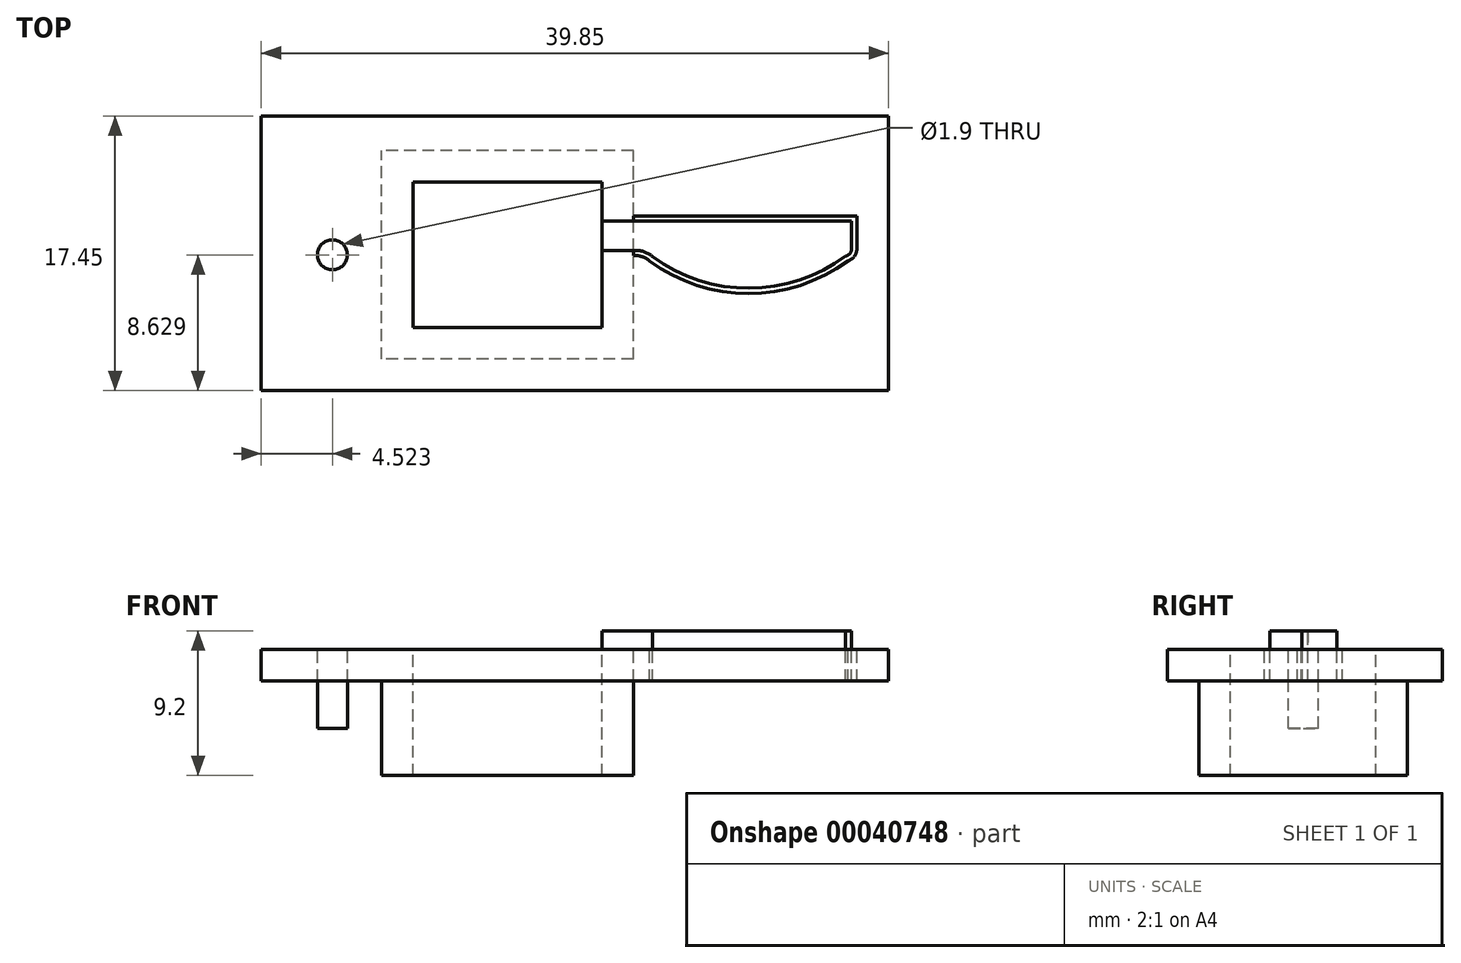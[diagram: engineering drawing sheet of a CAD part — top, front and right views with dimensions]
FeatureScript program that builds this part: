
annotation { "Feature Type Name" : "Feature", "Feature Type Description" : "" }
export const myFeature = defineFeature(function(context is Context, id is Id, definition is map)
    precondition{}
    {
        {
            var Q0;
            Q0=qCreatedBy(makeId("Top.planeOp"),FACE);
            var sketch = newSketch(context, id + "F0", { "sketchPlane" : qUnion([Q0])});
            skLineSegment(sketch, "E0", {"start": v(-14.38, 0) * mm, "end": v(14.38, 0) * mm});
            skLineSegment(sketch, "E1", {"start": v(14.38, 0) * mm, "end": v(14.38, -2.1) * mm});
            skLineSegment(sketch, "E2", {"start": v(-14.38, 0) * mm, "end": v(-14.38, -4.57) * mm});
            skLineSegment(sketch, "E3", {"start": v(-14.38, -4.57) * mm, "end": v(-4.8, -4.57) * mm});
            skLineSegment(sketch, "E4", {"start": v(-1.54, -2.52) * mm, "end": v(0.32, -2.52) * mm});
            skPoint(sketch, "E5", {"position": v(0, 0) * mm});
            skArc(sketch, "E6", {"start": v(-4.8, -4.57) * mm, "mid": v(-4.48, -4.53) * mm, "end": v(-4.18, -4.4) * mm});
            skArc(sketch, "E7", {"start": v(-1.54, -2.52) * mm, "mid": v(-2.14, -2.6) * mm, "end": v(-2.69, -2.86) * mm});
            skLineSegment(sketch, "E8", {"start": v(-4.18, -4.4) * mm, "end": v(-2.69, -2.86) * mm});
            skArc(sketch, "E9", {"start": v(0.32, -2.52) * mm, "mid": v(0.8, -2.6) * mm, "end": v(1.2, -2.85) * mm});
            skArc(sketch, "E10", {"start": v(1.2, -2.85) * mm, "mid": v(7.5, -4.93) * mm, "end": v(13.81, -2.85) * mm});
            skArc(sketch, "E11", {"start": v(14.38, -2.1) * mm, "mid": v(14.22, -2.57) * mm, "end": v(13.81, -2.85) * mm});
            skSolve(sketch);
        }
        {
            var Q0;
            Q0=qCreatedBy(makeId("Top.planeOp"),FACE);
            var sketch = newSketch(context, id + "F1", { "sketchPlane" : qUnion([Q0])});
            skLineSegment(sketch, "E12.rect.bottom", {"start": v(-1.81, -7.1) * mm, "end": v(-13.81, -7.1) * mm});
            skLineSegment(sketch, "E12.rect.top", {"start": v(-1.81, 2.15) * mm, "end": v(-13.81, 2.15) * mm});
            skLineSegment(sketch, "E12.rect.left", {"start": v(-1.81, -7.1) * mm, "end": v(-1.81, 2.15) * mm});
            skLineSegment(sketch, "E12.rect.right", {"start": v(-13.81, -7.1) * mm, "end": v(-13.81, 2.15) * mm});
            skPoint(sketch, "E12.rect.middle", {"position": v(-7.81, -2.47) * mm});
            skLineSegment(sketch, "E13.bottom", {"start": v(16.4, 6.35) * mm, "end": v(-23.45, 6.35) * mm});
            skLineSegment(sketch, "E13.top", {"start": v(16.4, -11.1) * mm, "end": v(-23.45, -11.1) * mm});
            skLineSegment(sketch, "E13.left", {"start": v(16.4, 6.35) * mm, "end": v(16.4, -11.1) * mm});
            skLineSegment(sketch, "E13.right", {"start": v(-23.45, 6.35) * mm, "end": v(-23.45, -11.1) * mm});
            skLineSegment(sketch, "E14.0.0", {"start": v(14.38, 0) * mm, "end": v(-14.38, 0) * mm});
            skLineSegment(sketch, "E14.0.1", {"start": v(-14.38, 0) * mm, "end": v(-14.38, -4.57) * mm});
            skLineSegment(sketch, "E14.0.2", {"start": v(-14.38, -4.57) * mm, "end": v(-4.8, -4.57) * mm});
            skArc(sketch, "E14.0.3", {"start": v(-4.8, -4.57) * mm, "mid": v(-4.48, -4.53) * mm, "end": v(-4.18, -4.4) * mm});
            skLineSegment(sketch, "E14.0.4", {"start": v(-4.18, -4.4) * mm, "end": v(-2.69, -2.86) * mm});
            skArc(sketch, "E14.0.5", {"start": v(-2.69, -2.86) * mm, "mid": v(-2.14, -2.6) * mm, "end": v(-1.54, -2.52) * mm});
            skLineSegment(sketch, "E14.0.6", {"start": v(-1.54, -2.52) * mm, "end": v(0.32, -2.52) * mm});
            skArc(sketch, "E14.0.7", {"start": v(0.32, -2.52) * mm, "mid": v(0.8, -2.6) * mm, "end": v(1.2, -2.85) * mm});
            skArc(sketch, "E14.0.8", {"start": v(1.2, -2.85) * mm, "mid": v(7.5, -4.93) * mm, "end": v(13.81, -2.85) * mm});
            skArc(sketch, "E14.0.9", {"start": v(13.81, -2.85) * mm, "mid": v(14.22, -2.57) * mm, "end": v(14.38, -2.1) * mm});
            skLineSegment(sketch, "E14.0.10", {"start": v(14.38, -2.1) * mm, "end": v(14.38, 0) * mm});
            skLineSegment(sketch, "E15.0", {"start": v(-14.05, -0.33) * mm, "end": v(-14.05, -4.24) * mm});
            skLineSegment(sketch, "E15.1", {"start": v(14.05, -0.33) * mm, "end": v(-14.05, -0.33) * mm});
            skLineSegment(sketch, "E15.2", {"start": v(14.05, -2.1) * mm, "end": v(14.05, -0.33) * mm});
            skArc(sketch, "E15.3", {"start": v(13.67, -2.55) * mm, "mid": v(13.94, -2.39) * mm, "end": v(14.05, -2.1) * mm});
            skArc(sketch, "E15.4", {"start": v(1.41, -2.6) * mm, "mid": v(7.55, -4.6) * mm, "end": v(13.67, -2.55) * mm});
            skLineSegment(sketch, "E15.5", {"start": v(-14.05, -4.24) * mm, "end": v(-4.8, -4.24) * mm});
            skArc(sketch, "E15.6", {"start": v(-4.8, -4.24) * mm, "mid": v(-4.37, -4.12) * mm, "end": v(-4.07, -3.8) * mm});
            skLineSegment(sketch, "E15.7", {"start": v(-4.07, -3.8) * mm, "end": v(-2.9, -2.6) * mm});
            skArc(sketch, "E15.8", {"start": v(-2.9, -2.6) * mm, "mid": v(-2.25, -2.3) * mm, "end": v(-1.54, -2.19) * mm});
            skLineSegment(sketch, "E15.9", {"start": v(-1.54, -2.19) * mm, "end": v(0.32, -2.19) * mm});
            skArc(sketch, "E15.10", {"start": v(0.32, -2.19) * mm, "mid": v(0.9, -2.3) * mm, "end": v(1.41, -2.6) * mm});
            skLineSegment(sketch, "E16.0", {"start": v(0.19, 4.15) * mm, "end": v(-15.81, 4.15) * mm});
            skLineSegment(sketch, "E16.1", {"start": v(0.19, -9.1) * mm, "end": v(0.19, 4.15) * mm});
            skLineSegment(sketch, "E16.2", {"start": v(0.19, -9.1) * mm, "end": v(-15.81, -9.1) * mm});
            skLineSegment(sketch, "E16.3", {"start": v(-15.81, -9.1) * mm, "end": v(-15.81, 4.15) * mm});
            skSolve(sketch);
        }
        {
            var Q0;
            {var subQ6=sQuery(id+"F1.wireOp",EDGE,"E15.2");Q0=makeQuery(id+"F1.imprint","IMPRINT",FACE,{"disambiguationData":[TD([[makeQuery(id+"F1.imprint","IMPRINT",EDGE,{"derivedFrom":subQ6}),1.0]])]});}
            var Q1;
            Q1=makeQuery(id+"F1.imprint","IMPRINT",FACE,{"disambiguationData":[TD([[makeQuery(id+"F1.imprint","IMPRINT",EDGE,{"derivedFrom":sQuery(id+"F1.wireOp",EDGE,"E13.bottom")}),1.0]])]});
            var Q2;
            {var subQ17=sQuery(id+"F1.wireOp",EDGE,"E12.rect.bottom");Q2=makeQuery(id+"F1.imprint","IMPRINT",FACE,{"disambiguationData":[TD([[makeQuery(id+"F1.imprint","IMPRINT",EDGE,{"derivedFrom":subQ17}),1.0]])]});}
            var Q3;
            {var subQ2=sQuery(id+"F1.wireOp",EDGE,"E12.rect.bottom");Q3=makeQuery(id+"F1.imprint","IMPRINT",FACE,{"disambiguationData":[TD([[makeQuery(id+"F1.imprint","IMPRINT",EDGE,{"derivedFrom":subQ2}),-1.0]])]});}
            var Q4;
            {var subQ5=sQuery(id+"F1.wireOp",EDGE,"E12.rect.top");Q4=makeQuery(id+"F1.imprint","IMPRINT",FACE,{"disambiguationData":[TD([[makeQuery(id+"F1.imprint","IMPRINT",EDGE,{"derivedFrom":subQ5}),1.0]])]});}
            var Q5;
            {var subQ1=sQuery(id+"F1.wireOp",EDGE,"E15.6");Q5=makeQuery(id+"F1.imprint","IMPRINT",FACE,{"disambiguationData":[TD([[makeQuery(id+"F1.imprint","IMPRINT",EDGE,{"derivedFrom":subQ1}),1.0]])]});}
            var Q6;
            {var subQ5=sQuery(id+"F1.wireOp",EDGE,"E15.8");var subQ7=sQuery(id+"F1.wireOp",EDGE,"E12.rect.left");var subQ9=makeQuery(id+"F1.imprint","INTERSECT",VERTEX,{"derivedFrom":[subQ7,subQ5]});Q6=makeQuery(id+"F1.imprint","IMPRINT",FACE,{"disambiguationData":[TD([[makeQuery(id+"F1.imprint","IMPRINT",EDGE,{"disambiguationData":[TD([[subQ9,-1.0]])],"derivedFrom":subQ7}),-1.0]])]});}
            var Q7;
            {var subQ0=sQuery(id+"F1.wireOp",EDGE,"E15.1");var subQ3=sQuery(id+"F1.wireOp",EDGE,"E12.rect.left");var subQ4=makeQuery(id+"F1.imprint","INTERSECT",VERTEX,{"derivedFrom":[subQ3,subQ0]});Q7=makeQuery(id+"F1.imprint","IMPRINT",FACE,{"disambiguationData":[TD([[makeQuery(id+"F1.imprint","IMPRINT",EDGE,{"disambiguationData":[TD([[subQ4,-1.0]])],"derivedFrom":subQ3}),-1.0]])]});}
            var Q8;
            {var subQ0=sQuery(id+"F1.wireOp",EDGE,"E15.1");var subQ3=sQuery(id+"F1.wireOp",EDGE,"E12.rect.left");var subQ4=makeQuery(id+"F1.imprint","INTERSECT",VERTEX,{"derivedFrom":[subQ3,subQ0]});Q8=makeQuery(id+"F1.imprint","IMPRINT",FACE,{"disambiguationData":[TD([[makeQuery(id+"F1.imprint","IMPRINT",EDGE,{"disambiguationData":[TD([[subQ4,-1.0]])],"derivedFrom":subQ3}),1.0]])]});}
            var Q9;
            {var subQ3=sQuery(id+"F1.wireOp",EDGE,"E15.0");Q9=makeQuery(id+"F1.imprint","IMPRINT",FACE,{"disambiguationData":[TD([[makeQuery(id+"F1.imprint","IMPRINT",EDGE,{"derivedFrom":subQ3}),1.0]])]});}
            var Q10;
            {var subQ10=sQuery(id+"F1.wireOp",EDGE,"E14.0.7");Q10=makeQuery(id+"F1.imprint","IMPRINT",FACE,{"disambiguationData":[TD([[makeQuery(id+"F1.imprint","IMPRINT",EDGE,{"derivedFrom":subQ10}),1.0]])]});}
            var Q11;
            {var subQ13=sQuery(id+"F1.wireOp",EDGE,"E14.0.3");Q11=makeQuery(id+"F1.imprint","IMPRINT",FACE,{"disambiguationData":[TD([[makeQuery(id+"F1.imprint","IMPRINT",EDGE,{"derivedFrom":subQ13}),1.0]])]});}
            var Q12;
            {var subQ6=sQuery(id+"F1.wireOp",EDGE,"E14.0.1");Q12=makeQuery(id+"F1.imprint","IMPRINT",FACE,{"disambiguationData":[TD([[makeQuery(id+"F1.imprint","IMPRINT",EDGE,{"derivedFrom":subQ6}),1.0]])]});}
            var Q13;
            {var subQ5=sQuery(id+"F1.wireOp",EDGE,"E12.rect.left");var subQ7=sQuery(id+"F1.wireOp",EDGE,"E14.0.5");var subQ8=makeQuery(id+"F1.imprint","INTERSECT",VERTEX,{"derivedFrom":[subQ5,subQ7]});Q13=makeQuery(id+"F1.imprint","IMPRINT",FACE,{"disambiguationData":[TD([[makeQuery(id+"F1.imprint","IMPRINT",EDGE,{"disambiguationData":[TD([[subQ8,-1.0]])],"derivedFrom":subQ5}),-1.0]])]});}
            extrude(context, id + "F2", {"entities" : qUnion([Q0, Q1, Q2, Q3, Q4, Q5, Q6, Q7, Q8, Q9, Q10, Q11, Q12, Q13]), "oppositeDirection" : true, "depth" : 2 * mm});
        }
        {
            var Q0;
            {var subQ17=sQuery(id+"F1.wireOp",EDGE,"E12.rect.bottom");Q0=makeQuery(id+"F1.imprint","IMPRINT",FACE,{"disambiguationData":[TD([[makeQuery(id+"F1.imprint","IMPRINT",EDGE,{"derivedFrom":subQ17}),1.0]])]});}
            var Q1;
            {var subQ1=sQuery(id+"F1.wireOp",EDGE,"E15.6");Q1=makeQuery(id+"F1.imprint","IMPRINT",FACE,{"disambiguationData":[TD([[makeQuery(id+"F1.imprint","IMPRINT",EDGE,{"derivedFrom":subQ1}),1.0]])]});}
            var Q2;
            {var subQ5=sQuery(id+"F1.wireOp",EDGE,"E15.8");var subQ7=sQuery(id+"F1.wireOp",EDGE,"E12.rect.left");var subQ9=makeQuery(id+"F1.imprint","INTERSECT",VERTEX,{"derivedFrom":[subQ7,subQ5]});Q2=makeQuery(id+"F1.imprint","IMPRINT",FACE,{"disambiguationData":[TD([[makeQuery(id+"F1.imprint","IMPRINT",EDGE,{"disambiguationData":[TD([[subQ9,-1.0]])],"derivedFrom":subQ7}),-1.0]])]});}
            var Q3;
            {var subQ0=sQuery(id+"F1.wireOp",EDGE,"E15.1");var subQ3=sQuery(id+"F1.wireOp",EDGE,"E12.rect.left");var subQ4=makeQuery(id+"F1.imprint","INTERSECT",VERTEX,{"derivedFrom":[subQ3,subQ0]});Q3=makeQuery(id+"F1.imprint","IMPRINT",FACE,{"disambiguationData":[TD([[makeQuery(id+"F1.imprint","IMPRINT",EDGE,{"disambiguationData":[TD([[subQ4,-1.0]])],"derivedFrom":subQ3}),-1.0]])]});}
            var Q4;
            {var subQ0=sQuery(id+"F1.wireOp",EDGE,"E15.1");var subQ3=sQuery(id+"F1.wireOp",EDGE,"E12.rect.left");var subQ4=makeQuery(id+"F1.imprint","INTERSECT",VERTEX,{"derivedFrom":[subQ3,subQ0]});Q4=makeQuery(id+"F1.imprint","IMPRINT",FACE,{"disambiguationData":[TD([[makeQuery(id+"F1.imprint","IMPRINT",EDGE,{"disambiguationData":[TD([[subQ4,-1.0]])],"derivedFrom":subQ3}),1.0]])]});}
            var Q5;
            {var subQ5=sQuery(id+"F1.wireOp",EDGE,"E12.rect.top");Q5=makeQuery(id+"F1.imprint","IMPRINT",FACE,{"disambiguationData":[TD([[makeQuery(id+"F1.imprint","IMPRINT",EDGE,{"derivedFrom":subQ5}),1.0]])]});}
            var Q6;
            {var subQ13=sQuery(id+"F1.wireOp",EDGE,"E14.0.3");Q6=makeQuery(id+"F1.imprint","IMPRINT",FACE,{"disambiguationData":[TD([[makeQuery(id+"F1.imprint","IMPRINT",EDGE,{"derivedFrom":subQ13}),1.0]])]});}
            var Q7;
            {var subQ2=sQuery(id+"F1.wireOp",EDGE,"E12.rect.bottom");Q7=makeQuery(id+"F1.imprint","IMPRINT",FACE,{"disambiguationData":[TD([[makeQuery(id+"F1.imprint","IMPRINT",EDGE,{"derivedFrom":subQ2}),-1.0]])]});}
            var Q8;
            {var subQ5=sQuery(id+"F1.wireOp",EDGE,"E12.rect.left");var subQ7=sQuery(id+"F1.wireOp",EDGE,"E14.0.5");var subQ8=makeQuery(id+"F1.imprint","INTERSECT",VERTEX,{"derivedFrom":[subQ5,subQ7]});Q8=makeQuery(id+"F1.imprint","IMPRINT",FACE,{"disambiguationData":[TD([[makeQuery(id+"F1.imprint","IMPRINT",EDGE,{"disambiguationData":[TD([[subQ8,-1.0]])],"derivedFrom":subQ5}),-1.0]])]});}
            var Q9;
            {var subQ6=sQuery(id+"F1.wireOp",EDGE,"E14.0.1");Q9=makeQuery(id+"F1.imprint","IMPRINT",FACE,{"disambiguationData":[TD([[makeQuery(id+"F1.imprint","IMPRINT",EDGE,{"derivedFrom":subQ6}),1.0]])]});}
            var Q10;
            {var subQ3=sQuery(id+"F1.wireOp",EDGE,"E15.0");Q10=makeQuery(id+"F1.imprint","IMPRINT",FACE,{"disambiguationData":[TD([[makeQuery(id+"F1.imprint","IMPRINT",EDGE,{"derivedFrom":subQ3}),1.0]])]});}
            extrude(context, id + "F3", {"entities" : qUnion([Q0, Q1, Q2, Q3, Q4, Q5, Q6, Q7, Q8, Q9, Q10]), "operationType" : NewBodyOperationType.ADD, "oppositeDirection" : true, "depth" : 8 * mm});
        }
        {
            var Q0;
            {var subQ1=sQuery(id+"F1.wireOp",EDGE,"E15.6");Q0=makeQuery(id+"F1.imprint","IMPRINT",FACE,{"disambiguationData":[TD([[makeQuery(id+"F1.imprint","IMPRINT",EDGE,{"derivedFrom":subQ1}),1.0]])]});}
            var Q1;
            {var subQ5=sQuery(id+"F1.wireOp",EDGE,"E15.8");var subQ7=sQuery(id+"F1.wireOp",EDGE,"E12.rect.left");var subQ9=makeQuery(id+"F1.imprint","INTERSECT",VERTEX,{"derivedFrom":[subQ7,subQ5]});Q1=makeQuery(id+"F1.imprint","IMPRINT",FACE,{"disambiguationData":[TD([[makeQuery(id+"F1.imprint","IMPRINT",EDGE,{"disambiguationData":[TD([[subQ9,-1.0]])],"derivedFrom":subQ7}),-1.0]])]});}
            var Q2;
            {var subQ6=sQuery(id+"F1.wireOp",EDGE,"E15.2");Q2=makeQuery(id+"F1.imprint","IMPRINT",FACE,{"disambiguationData":[TD([[makeQuery(id+"F1.imprint","IMPRINT",EDGE,{"derivedFrom":subQ6}),1.0]])]});}
            extrude(context, id + "F4", {"entities" : qUnion([Q0, Q1, Q2]), "operationType" : NewBodyOperationType.ADD, "depth" : 1.2 * mm});
        }
        {
            var Q0;
            {var subQ5=sQuery(id+"F1.wireOp",EDGE,"E12.rect.top");Q0=makeQuery(id+"F1.imprint","IMPRINT",FACE,{"disambiguationData":[TD([[makeQuery(id+"F1.imprint","IMPRINT",EDGE,{"derivedFrom":subQ5}),1.0]])]});}
            var Q1;
            {var subQ0=sQuery(id+"F1.wireOp",EDGE,"E15.1");var subQ3=sQuery(id+"F1.wireOp",EDGE,"E12.rect.left");var subQ4=makeQuery(id+"F1.imprint","INTERSECT",VERTEX,{"derivedFrom":[subQ3,subQ0]});Q1=makeQuery(id+"F1.imprint","IMPRINT",FACE,{"disambiguationData":[TD([[makeQuery(id+"F1.imprint","IMPRINT",EDGE,{"disambiguationData":[TD([[subQ4,-1.0]])],"derivedFrom":subQ3}),1.0]])]});}
            var Q2;
            {var subQ1=sQuery(id+"F1.wireOp",EDGE,"E15.6");Q2=makeQuery(id+"F1.imprint","IMPRINT",FACE,{"disambiguationData":[TD([[makeQuery(id+"F1.imprint","IMPRINT",EDGE,{"derivedFrom":subQ1}),1.0]])]});}
            var Q3;
            {var subQ2=sQuery(id+"F1.wireOp",EDGE,"E12.rect.bottom");Q3=makeQuery(id+"F1.imprint","IMPRINT",FACE,{"disambiguationData":[TD([[makeQuery(id+"F1.imprint","IMPRINT",EDGE,{"derivedFrom":subQ2}),-1.0]])]});}
            var Q4;
            {var subQ13=sQuery(id+"F1.wireOp",EDGE,"E14.0.3");Q4=makeQuery(id+"F1.imprint","IMPRINT",FACE,{"disambiguationData":[TD([[makeQuery(id+"F1.imprint","IMPRINT",EDGE,{"derivedFrom":subQ13}),1.0]])]});}
            extrude(context, id + "F5", {"entities" : qUnion([Q0, Q1, Q2, Q3, Q4]), "operationType" : NewBodyOperationType.REMOVE, "endBound" : BoundingType.SYMMETRIC, "oppositeDirection" : true, "depth" : 25 * mm});
        }
        {
            var Q0;
            Q0=makeQuery(id+"F2.opExtrude","CAP_FACE",FACE,{"disambiguationData":[OSD([sQuery(id+"F1.wireOp",EDGE,"E13.bottom"),sQuery(id+"F1.wireOp",EDGE,"E13.top"),sQuery(id+"F1.wireOp",EDGE,"E13.left"),sQuery(id+"F1.wireOp",EDGE,"E13.right")])],"isStart":true});
            var sketch = newSketch(context, id + "F6", { "sketchPlane" : qUnion([Q0])});
            skCircle(sketch, "E17", {"center": v(-18.93, -2.47) * mm, "radius": 0.95 * mm});
            skPoint(sketch, "E17.centerSnap0", {"position": v(-13.81, -2.47) * mm});
            skSolve(sketch);
        }
        {
            var Q0;
            Q0=makeQuery(id+"F6.imprint","IMPRINT",FACE,{"disambiguationData":[TD([[makeQuery(id+"F6.imprint","IMPRINT",EDGE,{"derivedFrom":sQuery(id+"F6.wireOp",EDGE,"E17")}),1.0]])]});
            extrude(context, id + "F7", {"entities" : qUnion([Q0]), "operationType" : NewBodyOperationType.REMOVE, "endBound" : BoundingType.THROUGH_ALL, "oppositeDirection" : true, "depth" : 25 * mm});
        }
        {
            var Q0;
            Q0=makeQuery(id+"F2.opExtrude","CAP_FACE",FACE,{"disambiguationData":[OSD([sQuery(id+"F1.wireOp",EDGE,"E13.bottom"),sQuery(id+"F1.wireOp",EDGE,"E13.top"),sQuery(id+"F1.wireOp",EDGE,"E13.left"),sQuery(id+"F1.wireOp",EDGE,"E13.right")])],"isStart":false});
            var sketch = newSketch(context, id + "F8", { "sketchPlane" : qUnion([Q0])});
            skCircle(sketch, "E18.0", {"center": v(-18.93, 2.47) * mm, "radius": 0.95 * mm});
            skCircle(sketch, "E19.0", {"center": v(-18.93, 2.47) * mm, "radius": 1.75 * mm});
            skSolve(sketch);
        }
        {
            var Q0;
            Q0=makeQuery(id+"F8.imprint","IMPRINT",FACE,{"disambiguationData":[TD([[makeQuery(id+"F8.imprint","IMPRINT",EDGE,{"derivedFrom":sQuery(id+"F8.wireOp",EDGE,"E18.0")}),1.0]])]});
            extrude(context, id + "F9", {"entities" : qUnion([Q0]), "operationType" : NewBodyOperationType.ADD, "depth" : 3 * mm});
        }
    });
